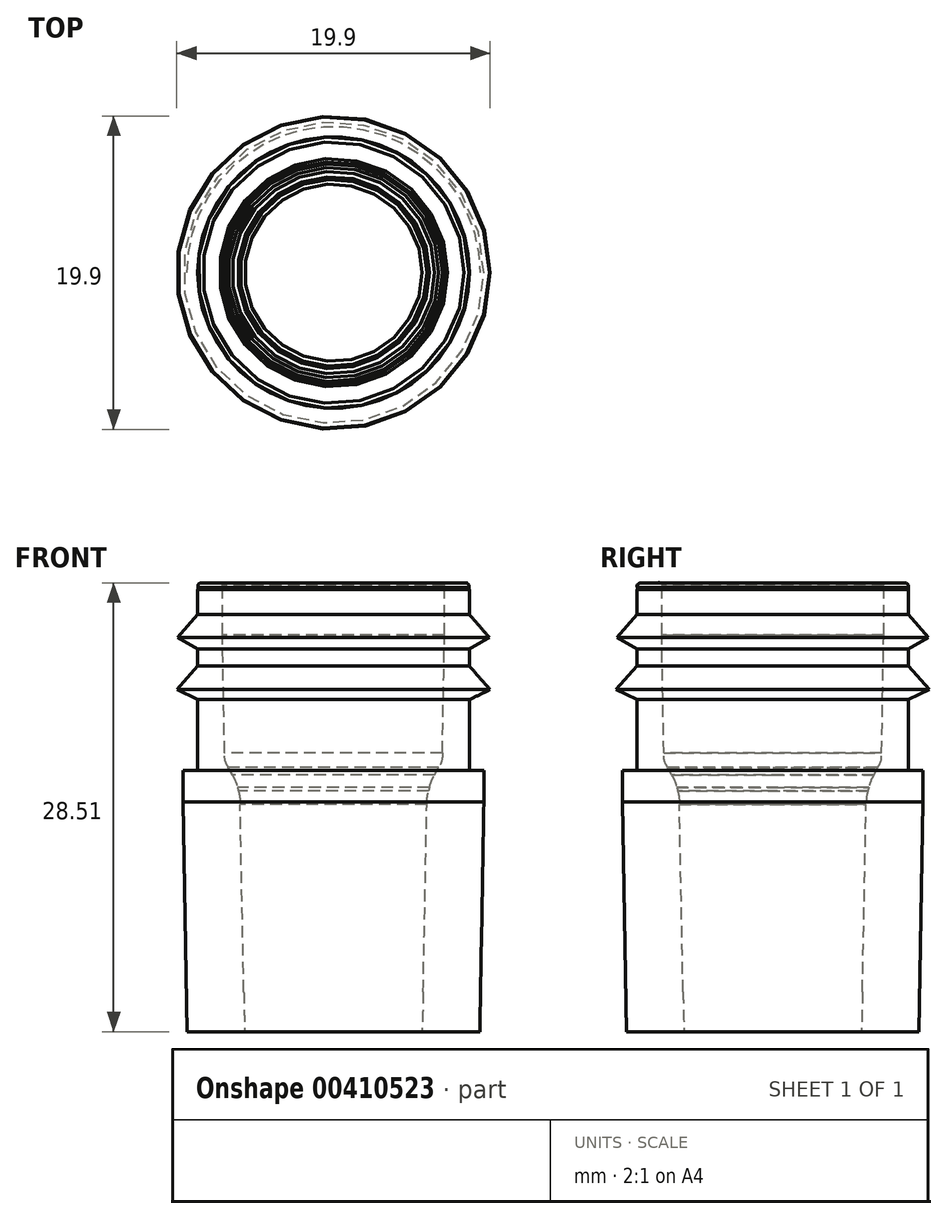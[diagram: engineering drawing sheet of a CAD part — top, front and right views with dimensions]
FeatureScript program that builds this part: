
annotation { "Feature Type Name" : "Feature", "Feature Type Description" : "" }
export const myFeature = defineFeature(function(context is Context, id is Id, definition is map)
    precondition{}
    {
        {
            var Q0;
            Q0=qCreatedBy(makeId("Front.planeOp"),FACE);
            var sketch = newSketch(context, id + "F0", { "sketchPlane" : qUnion([Q0])});
            skLineSegment(sketch, "E0", {"start": v(-3.36, 25.97) * mm, "end": v(-2.31, 25.97) * mm});
            skFitSpline(sketch, "E1", {"points": [v(-3.36, 25.97) * mm, v(-3.53, 25.97) * mm, v(-3.66, 25.84) * mm, v(-3.66, 25.67) * mm]});
            skLineSegment(sketch, "E2", {"start": v(-3.66, 25.57) * mm, "end": v(-3.66, 25.67) * mm});
            skLineSegment(sketch, "E3", {"start": v(-1.68, 14.15) * mm, "end": v(-1.74, 14.27) * mm});
            skLineSegment(sketch, "E4", {"start": v(-1.68, 14.15) * mm, "end": v(-1.49, 13.79) * mm});
            skLineSegment(sketch, "E5", {"start": v(-2.11, 25.77) * mm, "end": v(-2.11, 22.67) * mm});
            skFitSpline(sketch, "E6", {"points": [v(-2.11, 25.77) * mm, v(-2.11, 25.88) * mm, v(-2.2, 25.97) * mm, v(-2.31, 25.97) * mm]});
            skLineSegment(sketch, "E7", {"start": v(-2.11, 22.67) * mm, "end": v(-1.98, 15.17) * mm});
            skFitSpline(sketch, "E8", {"points": [v(-1.98, 15.17) * mm, v(-1.97, 14.86) * mm, v(-1.89, 14.55) * mm, v(-1.74, 14.27) * mm]});
            skFitSpline(sketch, "E9", {"points": [v(-1, 11.9) * mm, v(-1, 12.18) * mm, v(-1.03, 12.48) * mm, v(-1.1, 12.76) * mm]});
            skFitSpline(sketch, "E10", {"points": [v(-1.1, 12.76) * mm, v(-1.12, 12.83) * mm, v(-1.13, 12.9) * mm, v(-1.15, 12.97) * mm]});
            skFitSpline(sketch, "E11", {"points": [v(-1.15, 12.97) * mm, v(-1.24, 13.26) * mm, v(-1.35, 13.53) * mm, v(-1.49, 13.79) * mm]});
            skLineSegment(sketch, "E12", {"start": v(-1, 11.9) * mm, "end": v(-0.76, 0) * mm});
            skFitSpline(sketch, "E13", {"points": [v(-0.76, 0) * mm, v(-0.74, -0.89) * mm, v(-0.72, -1.77) * mm, v(-0.69, -2.66) * mm]});
            skLineSegment(sketch, "E14", {"start": v(-0.69, -2.66) * mm, "end": v(0.09, -26.1) * mm});
            skFitSpline(sketch, "E15", {"points": [v(2.44, -29.17) * mm, v(2.51, -29.22) * mm, v(2.59, -29.25) * mm, v(2.67, -29.28) * mm]});
            skFitSpline(sketch, "E16", {"points": [v(2.67, -29.28) * mm, v(2.7, -29.29) * mm, v(2.71, -29.3) * mm, v(2.73, -29.3) * mm]});
            skFitSpline(sketch, "E17", {"points": [v(2.73, -29.3) * mm, v(2.81, -29.32) * mm, v(2.9, -29.33) * mm, v(2.99, -29.33) * mm]});
            skFitSpline(sketch, "E18", {"points": [v(0.09, -26.1) * mm, v(0.12, -27.09) * mm, v(0.63, -28) * mm, v(1.45, -28.53) * mm]});
            skLineSegment(sketch, "E19", {"start": v(1.45, -28.53) * mm, "end": v(2.44, -29.17) * mm});
            skFitSpline(sketch, "E20", {"points": [v(2.67, -29.28) * mm, v(2.7, -29.29) * mm, v(2.71, -29.3) * mm, v(2.73, -29.3) * mm]});
            skLineSegment(sketch, "E21", {"start": v(-0.76, 0) * mm, "end": v(-0.69, -2.66) * mm});
            skLineSegment(sketch, "E22", {"start": v(-4.61, 12.07) * mm, "end": v(-4.61, 14.07) * mm});
            skLineSegment(sketch, "E23", {"start": v(-4.61, 12.07) * mm, "end": v(-3.95, -25.63) * mm});
            skArc(sketch, "E24", {"start": v(-3.95, -25.63) * mm, "mid": v(-3.23, -28) * mm, "end": v(-1.35, -29.63) * mm});
            skLineSegment(sketch, "E25", {"start": v(-1.35, -29.63) * mm, "end": v(1.24, -30.84) * mm});
            skLineSegment(sketch, "E26", {"start": v(3, -31.71) * mm, "end": v(3.94, -35.93) * mm});
            skLineSegment(sketch, "E27", {"start": v(-3.97, -24.63) * mm, "end": v(-4.2, -11.88) * mm});
            skLineSegment(sketch, "E28", {"start": v(-3.9, 18.8) * mm, "end": v(-3.85, 18.8) * mm});
            skLineSegment(sketch, "E29", {"start": v(-3.85, 18.8) * mm, "end": v(-3.81, 18.78) * mm});
            skLineSegment(sketch, "E30", {"start": v(-3.81, 18.78) * mm, "end": v(-3.78, 18.75) * mm});
            skLineSegment(sketch, "E31", {"start": v(-3.78, 18.75) * mm, "end": v(-3.75, 18.72) * mm});
            skLineSegment(sketch, "E32", {"start": v(-3.75, 18.72) * mm, "end": v(-3.72, 18.69) * mm});
            skLineSegment(sketch, "E33", {"start": v(-3.72, 18.69) * mm, "end": v(-3.7, 18.65) * mm});
            skLineSegment(sketch, "E34", {"start": v(-3.7, 18.65) * mm, "end": v(-3.7, 18.6) * mm});
            skLineSegment(sketch, "E35", {"start": v(-3.7, 18.6) * mm, "end": v(-3.69, 18.56) * mm});
            skLineSegment(sketch, "E36", {"start": v(-3.9, 22) * mm, "end": v(-3.85, 22) * mm});
            skLineSegment(sketch, "E37", {"start": v(-3.85, 22) * mm, "end": v(-3.81, 21.98) * mm});
            skLineSegment(sketch, "E38", {"start": v(-3.81, 21.98) * mm, "end": v(-3.78, 21.95) * mm});
            skLineSegment(sketch, "E39", {"start": v(-3.78, 21.95) * mm, "end": v(-3.75, 21.92) * mm});
            skLineSegment(sketch, "E40", {"start": v(-3.75, 21.92) * mm, "end": v(-3.72, 21.88) * mm});
            skLineSegment(sketch, "E41", {"start": v(-3.72, 21.88) * mm, "end": v(-3.7, 21.85) * mm});
            skLineSegment(sketch, "E42", {"start": v(-3.7, 21.85) * mm, "end": v(-3.7, 21.8) * mm});
            skLineSegment(sketch, "E43", {"start": v(-3.7, 21.8) * mm, "end": v(-3.69, 21.76) * mm});
            skLineSegment(sketch, "E44", {"start": v(-3.9, 18.8) * mm, "end": v(-4.19, 18.86) * mm});
            skLineSegment(sketch, "E45", {"start": v(-4.19, 18.86) * mm, "end": v(-4.48, 18.9) * mm});
            skLineSegment(sketch, "E46", {"start": v(-4.48, 18.9) * mm, "end": v(-4.78, 18.96) * mm});
            skLineSegment(sketch, "E47", {"start": v(-4.78, 18.96) * mm, "end": v(-4.8, 18.97) * mm});
            skLineSegment(sketch, "E48", {"start": v(-4.8, 18.97) * mm, "end": v(-4.84, 18.99) * mm});
            skLineSegment(sketch, "E49", {"start": v(-4.84, 18.99) * mm, "end": v(-4.87, 19) * mm});
            skLineSegment(sketch, "E50", {"start": v(-4.87, 19) * mm, "end": v(-4.9, 19.03) * mm});
            skLineSegment(sketch, "E51", {"start": v(-4.9, 19.03) * mm, "end": v(-4.91, 19.06) * mm});
            skLineSegment(sketch, "E52", {"start": v(-4.91, 19.06) * mm, "end": v(-4.93, 19.1) * mm});
            skLineSegment(sketch, "E53", {"start": v(-4.93, 19.1) * mm, "end": v(-4.94, 19.12) * mm});
            skLineSegment(sketch, "E54", {"start": v(-4.94, 19.12) * mm, "end": v(-4.94, 19.16) * mm});
            skLineSegment(sketch, "E55", {"start": v(-3.9, 22) * mm, "end": v(-4.18, 22.06) * mm});
            skLineSegment(sketch, "E56", {"start": v(-4.18, 22.06) * mm, "end": v(-4.48, 22.1) * mm});
            skLineSegment(sketch, "E57", {"start": v(-4.48, 22.1) * mm, "end": v(-4.78, 22.16) * mm});
            skLineSegment(sketch, "E58", {"start": v(-3.69, 23.97) * mm, "end": v(-3.69, 25.57) * mm});
            skLineSegment(sketch, "E59", {"start": v(-4.94, 19.16) * mm, "end": v(-4.94, 19.16) * mm});
            skLineSegment(sketch, "E60", {"start": v(-3.69, 20.77) * mm, "end": v(-3.69, 21.76) * mm});
            skLineSegment(sketch, "E61", {"start": v(-3.69, 14.07) * mm, "end": v(-3.69, 18.56) * mm});
            skLineSegment(sketch, "E62", {"start": v(-4.94, 19.2) * mm, "end": v(-4.94, 19.16) * mm});
            skLineSegment(sketch, "E63", {"start": v(-4.94, 22.36) * mm, "end": v(-4.94, 22.4) * mm});
            skLineSegment(sketch, "E64", {"start": v(-4.8, 22.76) * mm, "end": v(-4.45, 23.11) * mm});
            skLineSegment(sketch, "E65", {"start": v(-4.45, 23.11) * mm, "end": v(-4.1, 23.46) * mm});
            skLineSegment(sketch, "E66", {"start": v(-4.1, 23.46) * mm, "end": v(-3.76, 23.8) * mm});
            skLineSegment(sketch, "E67", {"start": v(-4.94, 22.4) * mm, "end": v(-4.94, 22.46) * mm});
            skLineSegment(sketch, "E68", {"start": v(-4.94, 22.46) * mm, "end": v(-4.93, 22.5) * mm});
            skLineSegment(sketch, "E69", {"start": v(-4.93, 22.5) * mm, "end": v(-4.92, 22.55) * mm});
            skLineSegment(sketch, "E70", {"start": v(-4.92, 22.55) * mm, "end": v(-4.9, 22.6) * mm});
            skLineSegment(sketch, "E71", {"start": v(-4.9, 22.6) * mm, "end": v(-4.88, 22.64) * mm});
            skLineSegment(sketch, "E72", {"start": v(-4.88, 22.64) * mm, "end": v(-4.86, 22.69) * mm});
            skLineSegment(sketch, "E73", {"start": v(-4.86, 22.69) * mm, "end": v(-4.83, 22.73) * mm});
            skLineSegment(sketch, "E74", {"start": v(-4.83, 22.73) * mm, "end": v(-4.8, 22.76) * mm});
            skLineSegment(sketch, "E75", {"start": v(-4.8, 19.56) * mm, "end": v(-4.45, 19.91) * mm});
            skLineSegment(sketch, "E76", {"start": v(-4.45, 19.91) * mm, "end": v(-4.1, 20.26) * mm});
            skLineSegment(sketch, "E77", {"start": v(-4.1, 20.26) * mm, "end": v(-3.76, 20.6) * mm});
            skLineSegment(sketch, "E78", {"start": v(-4.94, 19.2) * mm, "end": v(-4.94, 19.26) * mm});
            skLineSegment(sketch, "E79", {"start": v(-4.94, 19.26) * mm, "end": v(-4.93, 19.3) * mm});
            skLineSegment(sketch, "E80", {"start": v(-4.93, 19.3) * mm, "end": v(-4.92, 19.35) * mm});
            skLineSegment(sketch, "E81", {"start": v(-4.92, 19.35) * mm, "end": v(-4.9, 19.4) * mm});
            skLineSegment(sketch, "E82", {"start": v(-4.9, 19.4) * mm, "end": v(-4.88, 19.44) * mm});
            skLineSegment(sketch, "E83", {"start": v(-4.88, 19.44) * mm, "end": v(-4.86, 19.49) * mm});
            skLineSegment(sketch, "E84", {"start": v(-4.86, 19.49) * mm, "end": v(-4.83, 19.53) * mm});
            skLineSegment(sketch, "E85", {"start": v(-4.83, 19.53) * mm, "end": v(-4.8, 19.56) * mm});
            skLineSegment(sketch, "E86", {"start": v(-3.69, 23.97) * mm, "end": v(-3.7, 23.93) * mm});
            skLineSegment(sketch, "E87", {"start": v(-3.7, 23.93) * mm, "end": v(-3.7, 23.9) * mm});
            skLineSegment(sketch, "E88", {"start": v(-3.7, 23.9) * mm, "end": v(-3.71, 23.86) * mm});
            skLineSegment(sketch, "E89", {"start": v(-3.71, 23.86) * mm, "end": v(-3.73, 23.83) * mm});
            skLineSegment(sketch, "E90", {"start": v(-3.73, 23.83) * mm, "end": v(-3.76, 23.8) * mm});
            skLineSegment(sketch, "E91", {"start": v(-3.69, 20.77) * mm, "end": v(-3.7, 20.73) * mm});
            skLineSegment(sketch, "E92", {"start": v(-3.7, 20.73) * mm, "end": v(-3.7, 20.7) * mm});
            skLineSegment(sketch, "E93", {"start": v(-3.7, 20.7) * mm, "end": v(-3.71, 20.66) * mm});
            skLineSegment(sketch, "E94", {"start": v(-3.71, 20.66) * mm, "end": v(-3.73, 20.63) * mm});
            skLineSegment(sketch, "E95", {"start": v(-3.73, 20.63) * mm, "end": v(-3.76, 20.6) * mm});
            skLineSegment(sketch, "E96", {"start": v(1.66, -30.93) * mm, "end": v(2.03, -30.93) * mm});
            skLineSegment(sketch, "E97", {"start": v(-3.66, 25.57) * mm, "end": v(-3.69, 25.57) * mm});
            skLineSegment(sketch, "E98", {"start": v(-3.69, 14.07) * mm, "end": v(-4.61, 14.07) * mm});
            skLineSegment(sketch, "E99", {"start": v(4.94, -35.93) * mm, "end": v(4.94, 35.93) * mm});
            skLineSegment(sketch, "E100", {"start": v(4.94, -29.33) * mm, "end": v(2.99, -29.33) * mm});
            skLineSegment(sketch, "E101", {"start": v(4.94, -35.93) * mm, "end": v(3.94, -35.93) * mm});
            skSolve(sketch);
        }
        {
            var Q0;
            Q0=qCreatedBy(makeId("Front.planeOp"),FACE);
            var sketch = newSketch(context, id + "F1", { "sketchPlane" : qUnion([Q0])});
            skLineSegment(sketch, "E102.0", {"start": v(-1, 11.9) * mm, "end": v(-0.76, 0) * mm});
            skFitSpline(sketch, "E103.0", {"points": [v(-0.76, 0) * mm, v(-0.74, -0.89) * mm, v(-0.72, -1.77) * mm, v(-0.69, -2.66) * mm]});
            skLineSegment(sketch, "E104.0", {"start": v(-0.69, -2.66) * mm, "end": v(0.09, -26.1) * mm});
            skFitSpline(sketch, "E105.0", {"points": [v(0.09, -26.1) * mm, v(0.12, -27.09) * mm, v(0.63, -28) * mm, v(1.45, -28.53) * mm]});
            skLineSegment(sketch, "E106.0", {"start": v(1.45, -28.53) * mm, "end": v(2.44, -29.17) * mm});
            skFitSpline(sketch, "E107.0", {"points": [v(2.44, -29.17) * mm, v(2.51, -29.22) * mm, v(2.59, -29.25) * mm, v(2.67, -29.28) * mm]});
            skFitSpline(sketch, "E108.0", {"points": [v(2.67, -29.28) * mm, v(2.7, -29.29) * mm, v(2.71, -29.3) * mm, v(2.73, -29.3) * mm]});
            skFitSpline(sketch, "E109.0", {"points": [v(2.73, -29.3) * mm, v(2.81, -29.32) * mm, v(2.9, -29.33) * mm, v(2.99, -29.33) * mm]});
            skLineSegment(sketch, "E110.0", {"start": v(4.94, -29.33) * mm, "end": v(2.99, -29.33) * mm});
            skLineSegment(sketch, "E111.0", {"start": v(3, -31.71) * mm, "end": v(3.94, -35.93) * mm});
            skLineSegment(sketch, "E112.0", {"start": v(1.66, -30.93) * mm, "end": v(2.03, -30.93) * mm});
            skLineSegment(sketch, "E113.0", {"start": v(-1.35, -29.63) * mm, "end": v(1.24, -30.84) * mm});
            skArc(sketch, "E114.0", {"start": v(-3.95, -25.63) * mm, "mid": v(-3.23, -28) * mm, "end": v(-1.35, -29.63) * mm});
            skLineSegment(sketch, "E115.0", {"start": v(-4.61, 12.07) * mm, "end": v(-3.95, -25.63) * mm});
            skLineSegment(sketch, "E116.0", {"start": v(-4.61, 12.07) * mm, "end": v(-4.61, 14.07) * mm});
            skLineSegment(sketch, "E117.0", {"start": v(-3.69, 14.07) * mm, "end": v(-4.61, 14.07) * mm});
            skLineSegment(sketch, "E118.0", {"start": v(-3.69, 14.07) * mm, "end": v(-3.69, 18.56) * mm});
            skFitSpline(sketch, "E119.0", {"points": [v(-1, 11.9) * mm, v(-1, 12.18) * mm, v(-1.03, 12.48) * mm, v(-1.1, 12.76) * mm]});
            skFitSpline(sketch, "E120.0", {"points": [v(-1.1, 12.76) * mm, v(-1.12, 12.83) * mm, v(-1.13, 12.9) * mm, v(-1.15, 12.97) * mm]});
            skFitSpline(sketch, "E121.0", {"points": [v(-1.15, 12.97) * mm, v(-1.24, 13.26) * mm, v(-1.35, 13.53) * mm, v(-1.49, 13.79) * mm]});
            skLineSegment(sketch, "E122.0", {"start": v(-1.68, 14.15) * mm, "end": v(-1.49, 13.79) * mm});
            skLineSegment(sketch, "E123.0", {"start": v(-1.68, 14.15) * mm, "end": v(-1.74, 14.27) * mm});
            skFitSpline(sketch, "E124.0", {"points": [v(-1.98, 15.17) * mm, v(-1.97, 14.86) * mm, v(-1.89, 14.55) * mm, v(-1.74, 14.27) * mm]});
            skLineSegment(sketch, "E125.0", {"start": v(-2.11, 22.67) * mm, "end": v(-1.98, 15.17) * mm});
            skLineSegment(sketch, "E126.0", {"start": v(-2.11, 25.77) * mm, "end": v(-2.11, 22.67) * mm});
            skFitSpline(sketch, "E127.0", {"points": [v(-2.11, 25.77) * mm, v(-2.11, 25.88) * mm, v(-2.2, 25.97) * mm, v(-2.31, 25.97) * mm]});
            skLineSegment(sketch, "E128.0", {"start": v(-3.36, 25.97) * mm, "end": v(-2.31, 25.97) * mm});
            skFitSpline(sketch, "E129.0", {"points": [v(-3.36, 25.97) * mm, v(-3.53, 25.97) * mm, v(-3.66, 25.84) * mm, v(-3.66, 25.67) * mm]});
            skLineSegment(sketch, "E130.0", {"start": v(-3.66, 25.57) * mm, "end": v(-3.66, 25.67) * mm});
            skLineSegment(sketch, "E131.0", {"start": v(-3.66, 25.57) * mm, "end": v(-3.69, 25.57) * mm});
            skLineSegment(sketch, "E132.0", {"start": v(-3.69, 23.97) * mm, "end": v(-3.69, 25.57) * mm});
            skLineSegment(sketch, "E133", {"start": v(-3.69, 23.97) * mm, "end": v(-4.96, 22.5) * mm});
            skLineSegment(sketch, "E134", {"start": v(-4.96, 22.5) * mm, "end": v(-3.69, 21.77) * mm});
            skLineSegment(sketch, "E135", {"start": v(-3.69, 21.77) * mm, "end": v(-3.69, 20.7) * mm});
            skLineSegment(sketch, "E136", {"start": v(-3.69, 20.7) * mm, "end": v(-5, 19.2) * mm});
            skLineSegment(sketch, "E137", {"start": v(-5, 19.2) * mm, "end": v(-3.69, 18.56) * mm});
            skLineSegment(sketch, "E138.0", {"start": v(4.94, -35.93) * mm, "end": v(3.94, -35.93) * mm});
            skLineSegment(sketch, "E139", {"start": v(4.94, -29.33) * mm, "end": v(4.94, -35.93) * mm});
            skArc(sketch, "E140", {"start": v(3, -31.71) * mm, "mid": v(2.65, -31.15) * mm, "end": v(2.03, -30.93) * mm});
            skLineSegment(sketch, "E141", {"start": v(1.24, -30.84) * mm, "end": v(1.66, -30.93) * mm});
            skSolve(sketch);
        }
        {
            var Q0;
            Q0 = qSketchRegion(id + "F1", true);
            var Q1;
            Q1=sQuery(id+"F1.wireOp",EDGE,"E139");
            revolve(context, id + "F2", {"entities" : qUnion([Q0]), "axis" : qUnion([Q1]), "revolveType" : RevolveType.FULL});
        }
        {
            var Q0;
            Q0=qCreatedBy(makeId("Front.planeOp"),FACE);
            var sketch = newSketch(context, id + "F3", { "sketchPlane" : qUnion([Q0])});
            skLineSegment(sketch, "E142.top", {"start": v(-27.15, -48.25) * mm, "end": v(32.69, -48.25) * mm});
            skLineSegment(sketch, "E142.left", {"start": v(-27.15, -2.53) * mm, "end": v(-27.15, -48.25) * mm});
            skLineSegment(sketch, "E142.right", {"start": v(32.69, -2.53) * mm, "end": v(32.69, -48.25) * mm});
            skLineSegment(sketch, "E143", {"start": v(-3.36, 25.97) * mm, "end": v(-2.31, 25.97) * mm});
            skLineSegment(sketch, "E144", {"start": v(12.2, 25.97) * mm, "end": v(13.24, 25.97) * mm});
            skLineSegment(sketch, "E145", {"start": v(-27.15, -2.53) * mm, "end": v(32.69, -2.53) * mm});
            skLineSegment(sketch, "E146", {"start": v(-2.31, 25.97) * mm, "end": v(12.2, 25.97) * mm});
            skSolve(sketch);
        }
        {
            var Q0;
            Q0=makeQuery(id+"F3.imprint","IMPRINT",FACE,{"disambiguationData":[TD([[makeQuery(id+"F3.imprint","IMPRINT",EDGE,{"derivedFrom":sQuery(id+"F3.wireOp",EDGE,"E142.top")}),1.0]])]});
            extrude(context, id + "F4", {"entities" : qUnion([Q0]), "operationType" : NewBodyOperationType.REMOVE, "endBound" : BoundingType.THROUGH_ALL, "oppositeDirection" : true, "depth" : 50 * mm, "hasSecondDirection" : true, "secondDirectionBound" : SecondDirectionBoundingType.THROUGH_ALL, "secondDirectionOppositeDirection" : false, "secondDirectionDepth" : 25 * mm});
        }
    });
